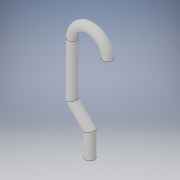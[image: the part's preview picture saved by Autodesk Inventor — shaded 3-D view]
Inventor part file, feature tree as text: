
AUTODESK INVENTOR PART (.ipt)
format: ipt  version: 2019.1 (Build 231200000, 200)  size: 125,440 bytes
history: native  units: in
note: dims shown in document units (in); Inventor stores cm internally (conversion verified against a paired STEP export)
features: sketch x3, sweep x1, hole x1
ambient origin geometry x8: Origin, YZ Plane, XZ Plane, XY Plane, X Axis, Y Axis, Z Axis, Center Point
bodies: Solid1 (feature_tree)
feature tree (5):
  sweep  "Sweep1"
  hole  "Hole1"  [1 undecoded]
  sketch  "Sketch1"  dims[d1=0.75in d2=45.0deg]
  sketch  "Sketch2"  dims[d5=1.0in d6=4.0in]
  sketch  "Sketch3"  dims[d7=0.375in d8=0.0in d9=0.0in d10=0.196in d11=0.5in d12=0.256in d13=0.118in d14=0.5635in d15=0.75in d16=0.8108in]
note: 1 required parameter value undecoded (feature->parameter linkage not recoverable at this tier; creation-order binding heuristic only, values carry confidence <= 0.55)
